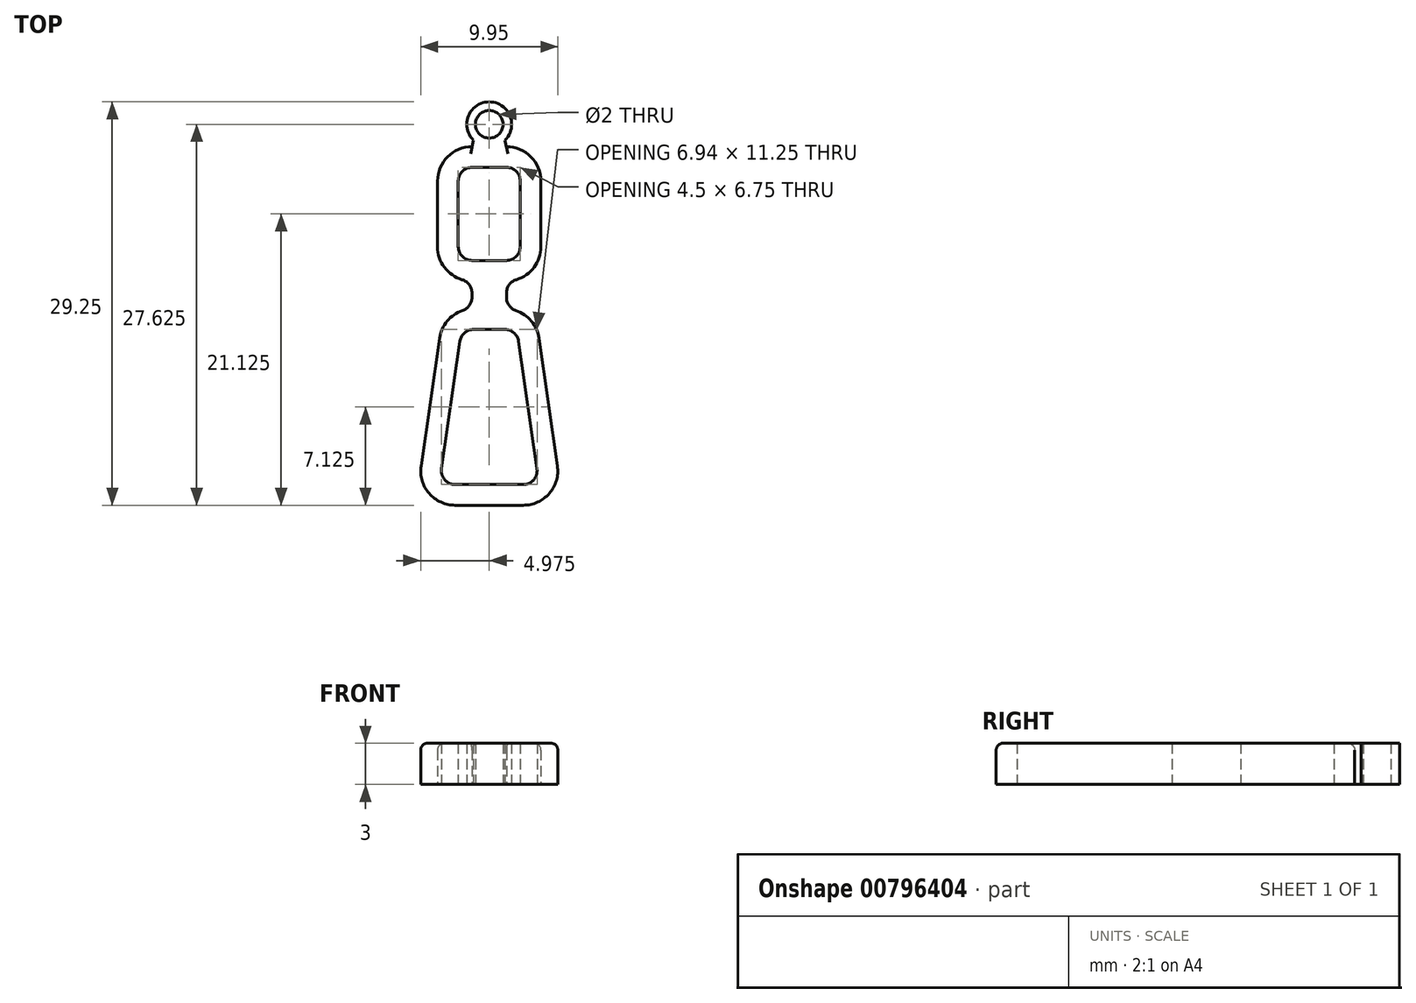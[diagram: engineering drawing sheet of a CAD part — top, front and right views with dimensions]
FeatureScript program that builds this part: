
annotation { "Feature Type Name" : "Feature", "Feature Type Description" : "" }
export const myFeature = defineFeature(function(context is Context, id is Id, definition is map)
    precondition{}
    {
        {
            var Q0;
            Q0=qCreatedBy(makeId("Top.planeOp"),FACE);
            var sketch = newSketch(context, id + "F0", { "sketchPlane" : qUnion([Q0])});
            skLineSegment(sketch, "E0", {"start": v(1.15, 0) * mm, "end": v(6.1, 0) * mm});
            skLineSegment(sketch, "E1.MirrorCS", {"start": v(5.75, 10.4) * mm, "end": v(7.08, 1.14) * mm});
            skLineSegment(sketch, "E2.MirrorCS", {"start": v(1.5, 10.4) * mm, "end": v(0.17, 1.14) * mm});
            skLineSegment(sketch, "E3.MirrorCS", {"start": v(2.5, 11.25) * mm, "end": v(4.76, 11.25) * mm});
            skLineSegment(sketch, "E4", {"start": v(5.88, 17.25) * mm, "end": v(5.88, 22) * mm});
            skLineSegment(sketch, "E5.MirrorCS", {"start": v(1.38, 17.25) * mm, "end": v(1.38, 22) * mm});
            skLineSegment(sketch, "E6", {"start": v(4.88, 23) * mm, "end": v(2.38, 23) * mm});
            skLineSegment(sketch, "E7", {"start": v(4.88, 16.25) * mm, "end": v(2.38, 16.25) * mm});
            skLineSegment(sketch, "E8", {"start": v(3.63, 16.25) * mm, "end": v(3.63, 11.25) * mm});
            skPoint(sketch, "E9.visualSharp", {"position": v(5.88, 23) * mm});
            skArc(sketch, "E9.filletArc", {"start": v(5.88, 22) * mm, "mid": v(5.58, 22.7) * mm, "end": v(4.88, 23) * mm});
            skPoint(sketch, "E10.visualSharp", {"position": v(1.38, 23) * mm});
            skArc(sketch, "E10.filletArc", {"start": v(2.38, 23) * mm, "mid": v(1.67, 22.7) * mm, "end": v(1.38, 22) * mm});
            skPoint(sketch, "E11.visualSharp", {"position": v(5.88, 16.25) * mm});
            skArc(sketch, "E11.filletArc", {"start": v(4.88, 16.25) * mm, "mid": v(5.58, 16.54) * mm, "end": v(5.88, 17.25) * mm});
            skPoint(sketch, "E12.visualSharp", {"position": v(1.38, 16.25) * mm});
            skArc(sketch, "E12.filletArc", {"start": v(1.38, 17.25) * mm, "mid": v(1.67, 16.54) * mm, "end": v(2.38, 16.25) * mm});
            skPoint(sketch, "E13.visualSharp", {"position": v(7.25, 0) * mm});
            skArc(sketch, "E13.filletArc", {"start": v(6.1, 0) * mm, "mid": v(6.85, 0.35) * mm, "end": v(7.08, 1.14) * mm});
            skPoint(sketch, "E14.visualSharp", {"position": v(0, 0) * mm});
            skArc(sketch, "E14.filletArc", {"start": v(0.17, 1.14) * mm, "mid": v(0.4, 0.35) * mm, "end": v(1.15, 0) * mm});
            skPoint(sketch, "E15.visualSharp", {"position": v(5.63, 11.25) * mm});
            skArc(sketch, "E15.filletArc", {"start": v(5.75, 10.4) * mm, "mid": v(5.41, 11) * mm, "end": v(4.76, 11.25) * mm});
            skPoint(sketch, "E16.visualSharp", {"position": v(1.63, 11.25) * mm});
            skArc(sketch, "E16.filletArc", {"start": v(2.5, 11.25) * mm, "mid": v(1.84, 11) * mm, "end": v(1.5, 10.4) * mm});
            skLineSegment(sketch, "E17.0", {"start": v(-0.13, 17.25) * mm, "end": v(-0.13, 22) * mm});
            skLineSegment(sketch, "E17.1", {"start": v(7.38, 17.25) * mm, "end": v(7.38, 22) * mm});
            skArc(sketch, "E17.2", {"start": v(7.38, 22) * mm, "mid": v(6.64, 23.77) * mm, "end": v(4.88, 24.5) * mm});
            skArc(sketch, "E17.4", {"start": v(2.38, 24.5) * mm, "mid": v(0.6, 23.77) * mm, "end": v(-0.13, 22) * mm});
            skLineSegment(sketch, "E18.0", {"start": v(7.23, 10.6) * mm, "end": v(8.57, 1.36) * mm});
            skLineSegment(sketch, "E18.1", {"start": v(0.02, 10.6) * mm, "end": v(-1.32, 1.36) * mm});
            skArc(sketch, "E18.2", {"start": v(-1.32, 1.36) * mm, "mid": v(-0.74, -0.64) * mm, "end": v(1.15, -1.5) * mm});
            skLineSegment(sketch, "E18.3", {"start": v(1.15, -1.5) * mm, "end": v(6.1, -1.5) * mm});
            skArc(sketch, "E18.4", {"start": v(6.1, -1.5) * mm, "mid": v(7.99, -0.64) * mm, "end": v(8.57, 1.36) * mm});
            skArc(sketch, "E19.0", {"start": v(7.23, 10.6) * mm, "mid": v(6.68, 11.85) * mm, "end": v(5.56, 12.62) * mm});
            skArc(sketch, "E20.0", {"start": v(1.7, 12.62) * mm, "mid": v(0.57, 11.85) * mm, "end": v(0.02, 10.6) * mm});
            skArc(sketch, "E21.0", {"start": v(-0.12, 17.25) * mm, "mid": v(0.37, 15.76) * mm, "end": v(1.66, 14.85) * mm});
            skArc(sketch, "E22.0", {"start": v(5.59, 14.85) * mm, "mid": v(6.88, 15.76) * mm, "end": v(7.38, 17.25) * mm});
            skLineSegment(sketch, "E23", {"start": v(2.38, 13.9) * mm, "end": v(2.38, 13.57) * mm});
            skLineSegment(sketch, "E24", {"start": v(4.87, 13.9) * mm, "end": v(4.87, 13.57) * mm});
            skPoint(sketch, "E25.visualSharp", {"position": v(4.87, 12.75) * mm});
            skArc(sketch, "E25.filletArc", {"start": v(4.87, 13.57) * mm, "mid": v(5.06, 12.98) * mm, "end": v(5.56, 12.62) * mm});
            skPoint(sketch, "E26.visualSharp", {"position": v(2.38, 12.75) * mm});
            skArc(sketch, "E26.filletArc", {"start": v(1.7, 12.62) * mm, "mid": v(2.19, 12.98) * mm, "end": v(2.38, 13.57) * mm});
            skPoint(sketch, "E27.visualSharp", {"position": v(2.38, 14.75) * mm});
            skArc(sketch, "E27.filletArc", {"start": v(2.38, 13.9) * mm, "mid": v(2.18, 14.5) * mm, "end": v(1.66, 14.85) * mm});
            skPoint(sketch, "E28.visualSharp", {"position": v(4.87, 14.75) * mm});
            skArc(sketch, "E28.filletArc", {"start": v(5.59, 14.85) * mm, "mid": v(5.07, 14.5) * mm, "end": v(4.87, 13.9) * mm});
            skArc(sketch, "E29", {"start": v(4.77, 24.98) * mm, "mid": v(3.63, 27.75) * mm, "end": v(2.48, 24.98) * mm});
            skCircle(sketch, "E30", {"center": v(3.63, 26.13) * mm, "radius": 1 * mm});
            skLineSegment(sketch, "E31", {"start": v(2.48, 24.98) * mm, "end": v(2.38, 24.5) * mm});
            skLineSegment(sketch, "E32.MirrorCS", {"start": v(4.77, 24.98) * mm, "end": v(4.88, 24.5) * mm});
            skSolve(sketch);
        }
        {
            var Q0;
            Q0=makeQuery(id+"F0.imprint","IMPRINT",FACE,{"disambiguationData":[TD([[makeQuery(id+"F0.imprint","IMPRINT",EDGE,{"derivedFrom":sQuery(id+"F0.wireOp",EDGE,"E0")}),-1.0]])]});
            extrude(context, id + "F1", {"entities" : qUnion([Q0]), "depth" : 3 * mm, "offsetDistance" : 25 * mm});
        }
        {
            var Q0;
            Q0=makeQuery(id+"F1.opExtrude","CAP_EDGE",EDGE,{"disambiguationData":[OSD([sQuery(id+"F0.wireOp",EDGE,"E18.0")])],"isStart":false});
            fillet(context, id + "F2", {"entities" : qUnion([Q0]), "radius" : .5 * mm, "tangentPropagation" : true, "allowEdgeOverflow" : false});
        }
    });
